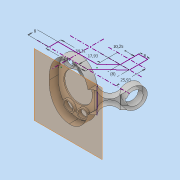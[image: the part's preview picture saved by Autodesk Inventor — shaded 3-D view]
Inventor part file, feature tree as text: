
AUTODESK INVENTOR PART (.ipt)
format: ipt  version: 2019 (Build 230136000, 136)  size: 544,256 bytes
history: native  units: mm
features: other x22, sketch x8, extrude x5, loft x3, projected_geometry x2, shell x1
ambient origin geometry x8: Origin, YZ Plane, XZ Plane, XY Plane, X Axis, Y Axis, Z Axis, Center Point
bodies: Body1 (feature_tree), Body2 (feature_tree), Body3 (feature_tree), Body4 (feature_tree)
feature tree (41):
  other  "Твердое тело1"
  other  "Основной эскиз"
  extrude  "ВыдавливаниеОсновной"  Depth=34.31mm
  other  "РабПлоскость18"
  other  "РабПлоскость41"
  other  "Ручка"
  other  "РабПлоскость42"
  other  "РабПлоскость43"
  loft  "Лофт15"
  extrude  "Выдавливание32"  Depth=34.31mm
  sketch  "Эскиз37"
  other  "РабПлоскость45"
  extrude  "Выдавливание35"  Depth=8.0mm
  extrude  "Корпус элипса"  Depth=17.93mm
  extrude  "Дырки"  Depth=25.93mm
  loft  "Лофт25"
  sketch  "Эскиз43"
  sketch  "Эскиз44"
  other  "РабПлоскость46"
  loft  "Лофт27"
  shell  "Оболочка15"  Thickness=49.49mm
  other  "Удаление грани34"
  other  "Удаление грани35"
  other  "Удаление грани36"
  other  "Удаление грани37"
  other  "Удаление грани38"
  other  "Удаление грани39"
  other  "Отвертстия"
  other  "Твердое тело13"
  sketch  "Эскиз33"
  sketch  "Эскиз34"
  other  "Твердое тело18"
  sketch  "Эскиз38"
  other  "Твердое тело24"
  sketch  "Эскиз42"
  other  "Ребра55"
  other  "Ребра56"
  projected_geometry  "Спроецированная петля7"
  sketch  "Эскиз46"
  projected_geometry  "Спроецированная петля8"
  other  "Ребра57"
